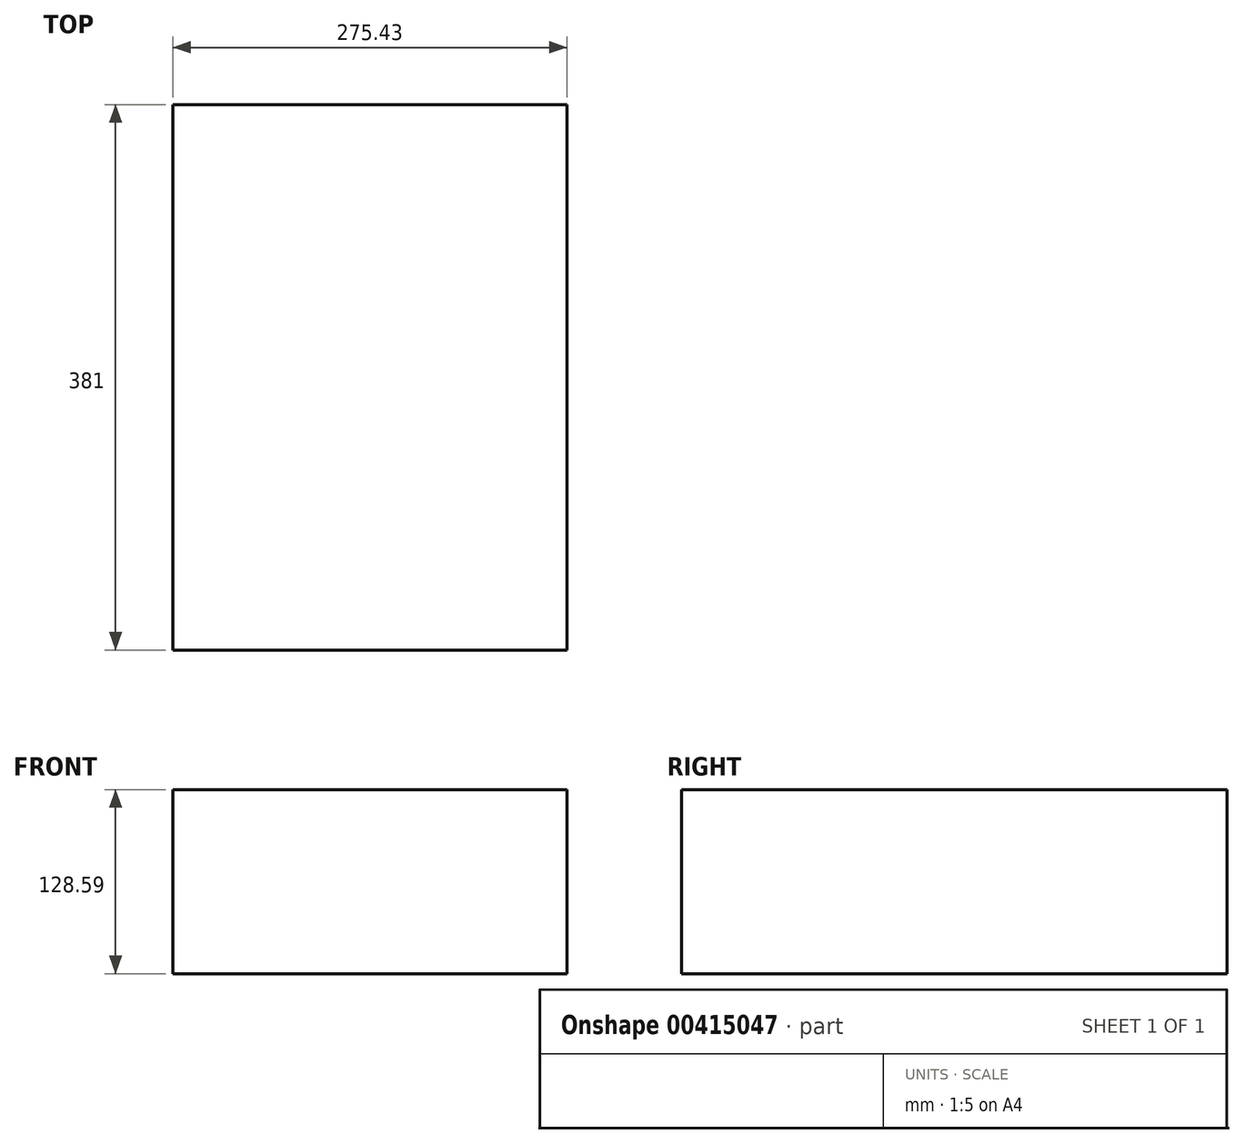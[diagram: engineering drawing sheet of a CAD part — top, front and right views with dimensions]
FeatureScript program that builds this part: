
annotation { "Feature Type Name" : "Feature", "Feature Type Description" : "" }
export const myFeature = defineFeature(function(context is Context, id is Id, definition is map)
    precondition{}
    {
        {
            var Q0;
            Q0=qCreatedBy(makeId("Front.planeOp"),FACE);
            var sketch = newSketch(context, id + "F0", { "sketchPlane" : qUnion([Q0])});
            skLineSegment(sketch, "E0.bottom", {"start": v(0, 0) * mm, "end": v(275.43, 0) * mm});
            skLineSegment(sketch, "E0.top", {"start": v(0, 128.59) * mm, "end": v(275.43, 128.59) * mm});
            skLineSegment(sketch, "E0.left", {"start": v(0, 0) * mm, "end": v(0, 128.59) * mm});
            skLineSegment(sketch, "E0.right", {"start": v(275.43, 0) * mm, "end": v(275.43, 128.59) * mm});
            skSolve(sketch);
        }
        {
            var Q0;
            Q0=makeQuery(id+"F0.imprint","IMPRINT",FACE,{"disambiguationData":[TD([[makeQuery(id+"F0.imprint","IMPRINT",EDGE,{"derivedFrom":sQuery(id+"F0.wireOp",EDGE,"E0.bottom")}),1.0]])]});
            extrude(context, id + "F1", {"entities" : qUnion([Q0]), "depth" : 381 * mm, "offsetDistance" : 25.4 * mm});
        }
    });
